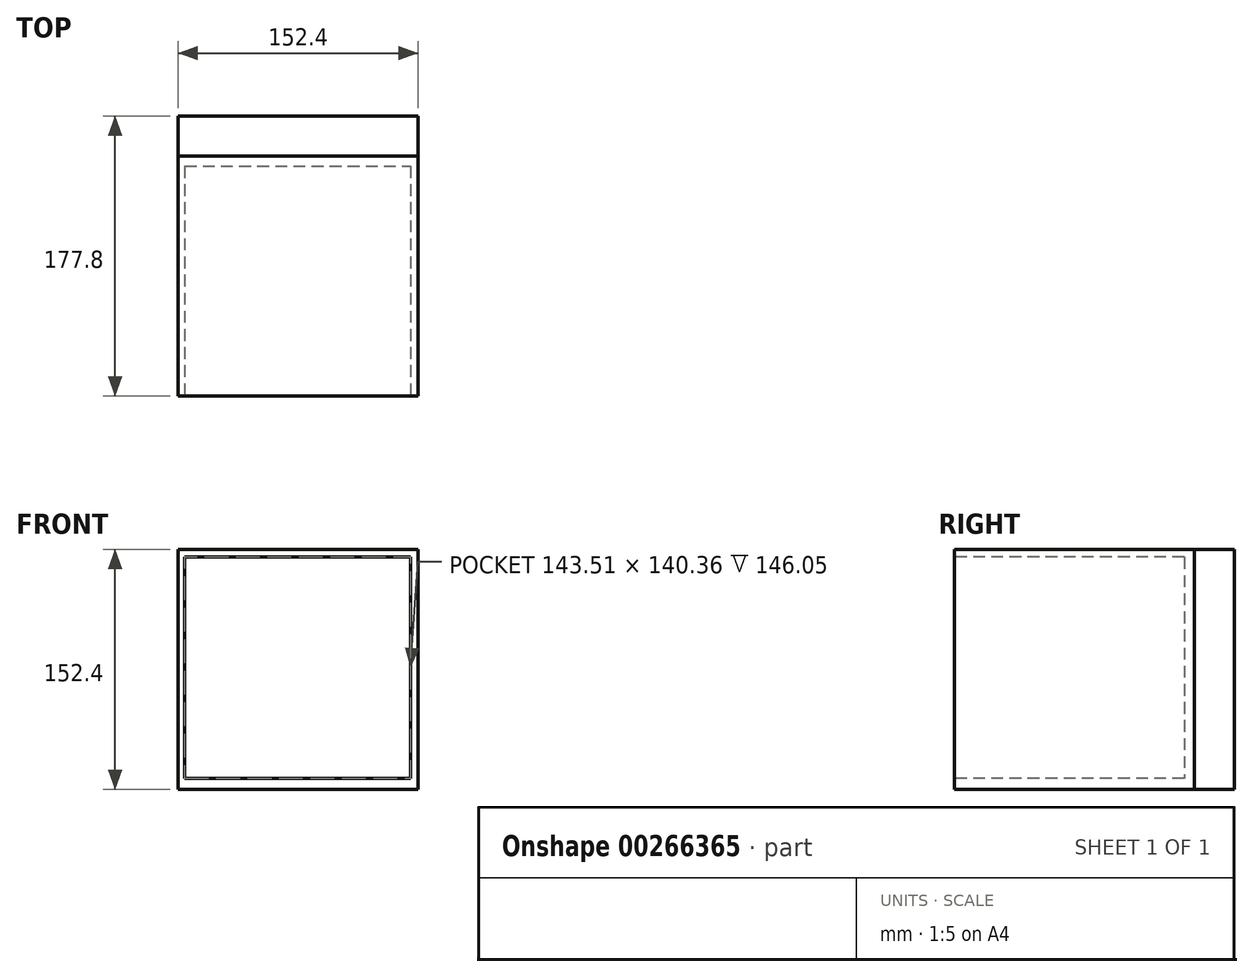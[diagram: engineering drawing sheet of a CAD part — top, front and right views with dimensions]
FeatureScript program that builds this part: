
annotation { "Feature Type Name" : "Feature", "Feature Type Description" : "" }
export const myFeature = defineFeature(function(context is Context, id is Id, definition is map)
    precondition{}
    {
        {
            var Q0;
            Q0=qCreatedBy(makeId("Front.planeOp"),FACE);
            var sketch = newSketch(context, id + "F0", { "sketchPlane" : qUnion([Q0])});
            skLineSegment(sketch, "E0.bottom", {"start": v(0, 0) * mm, "end": v(-152.4, 0) * mm});
            skLineSegment(sketch, "E0.top", {"start": v(0, 152.4) * mm, "end": v(-152.4, 152.4) * mm});
            skLineSegment(sketch, "E0.left", {"start": v(0, 0) * mm, "end": v(0, 152.4) * mm});
            skLineSegment(sketch, "E0.right", {"start": v(-152.4, 0) * mm, "end": v(-152.4, 152.4) * mm});
            skSolve(sketch);
        }
        {
            var Q0;
            Q0 = qSketchRegion(id + "F0", true);
            extrude(context, id + "F1", {"entities" : qUnion([Q0]), "depth" : 25.4 * mm});
        }
        {
            var Q0;
            Q0=makeQuery(id+"F1.opExtrude","CAP_FACE",FACE,{"disambiguationData":[OSD([sQuery(id+"F0.wireOp",EDGE,"E0.bottom"),sQuery(id+"F0.wireOp",EDGE,"E0.top"),sQuery(id+"F0.wireOp",EDGE,"E0.left"),sQuery(id+"F0.wireOp",EDGE,"E0.right")])],"isStart":false});
            extrude(context, id + "F2", {"entities" : qUnion([Q0]), "depth" : 152.4 * mm});
        }
        {
            var Q0;
            Q0=makeQuery(id+"F2.opExtrude","CAP_FACE",FACE,{"disambiguationData":[OSD([sQuery(id+"F0.wireOp",EDGE,"E0.bottom"),sQuery(id+"F0.wireOp",EDGE,"E0.top"),sQuery(id+"F0.wireOp",EDGE,"E0.left"),sQuery(id+"F0.wireOp",EDGE,"E0.right")])],"isStart":false});
            var sketch = newSketch(context, id + "F3", { "sketchPlane" : qUnion([Q0])});
            skLineSegment(sketch, "E1.bottom", {"start": v(-148.1, 147.53) * mm, "end": v(-4.59, 147.53) * mm});
            skLineSegment(sketch, "E1.top", {"start": v(-148.1, 7.17) * mm, "end": v(-4.59, 7.17) * mm});
            skLineSegment(sketch, "E1.left", {"start": v(-148.1, 147.53) * mm, "end": v(-148.1, 7.17) * mm});
            skLineSegment(sketch, "E1.right", {"start": v(-4.59, 147.53) * mm, "end": v(-4.59, 7.17) * mm});
            skSolve(sketch);
        }
        {
            var Q0;
            Q0 = qSketchRegion(id + "F3", true);
            extrude(context, id + "F4", {"entities" : qUnion([Q0]), "operationType" : NewBodyOperationType.REMOVE, "oppositeDirection" : true, "depth" : 146.05 * mm});
        }
    });
